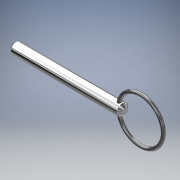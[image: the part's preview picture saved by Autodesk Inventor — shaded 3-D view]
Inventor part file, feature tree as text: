
AUTODESK INVENTOR PART (.ipt)
format: ipt  version: 2019 (Build 230136000, 136)  size: 167,936 bytes
history: native  units: in
note: dims shown in document units (in); Inventor stores cm internally (conversion verified against a paired STEP export)
features: sketch x5, extrude x2, sweep x1, revolve x1, chamfer x1
ambient origin geometry x8: Origin, YZ Plane, XZ Plane, XY Plane, X Axis, Y Axis, Z Axis, Center Point
bodies: Solid1 (feature_tree)
feature tree (10):
  extrude  "Extrusion1"  Depth=2.5in TaperAngle=0.0deg
  extrude  "Extrusion2"  Depth=0.125in
  sweep  "Sweep1"
  revolve  "Revolution1"  [1 undecoded]
  chamfer  "Chamfer1"  [1 undecoded]
  sketch  "Sketch1"  dims[d0=0.25in d1=2.5in d2=0.0in]
  sketch  "Sketch2"  dims[d3=0.1in d4=0.125in]
  sketch  "Sketch3"  dims[d5=2.5in d6=0.0in d7=1.0in]
  sketch  "Sketch4"  dims[d8=1.6in d9=0.08in d10=0.0in d11=0.0in]
  sketch  "Sketch5"  dims[d12=0.0625in d13=0.125in d14=0.0312in d15=90.0deg d16=0.0625in d17=0.125in d18=45.0deg]
note: 2 required parameter values undecoded (feature->parameter linkage not recoverable at this tier; creation-order binding heuristic only, values carry confidence <= 0.55)